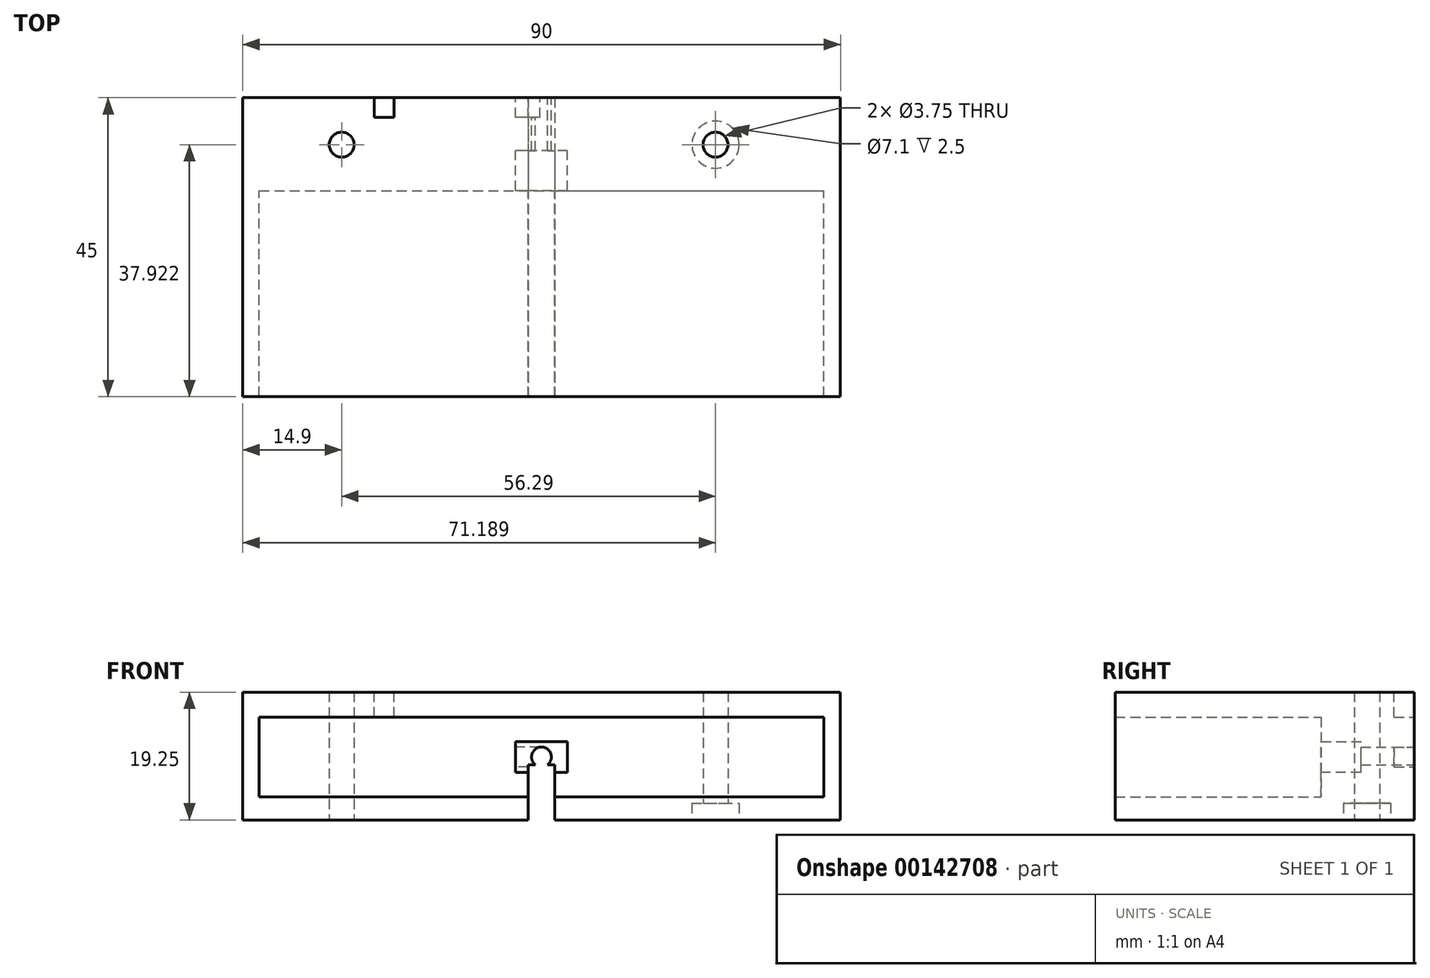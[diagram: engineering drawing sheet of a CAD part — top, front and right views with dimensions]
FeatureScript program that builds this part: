
annotation { "Feature Type Name" : "Feature", "Feature Type Description" : "" }
export const myFeature = defineFeature(function(context is Context, id is Id, definition is map)
    precondition{}
    {
        {
            var Q0;
            Q0=qCreatedBy(makeId("Front.planeOp"),FACE);
            var sketch = newSketch(context, id + "F0", { "sketchPlane" : qUnion([Q0])});
            skLineSegment(sketch, "E0.bottom", {"start": v(-59.7, 43.79) * mm, "end": v(25.3, 43.79) * mm});
            skLineSegment(sketch, "E0.top", {"start": v(-59.7, 31.79) * mm, "end": v(25.3, 31.79) * mm});
            skLineSegment(sketch, "E0.left", {"start": v(-59.7, 43.79) * mm, "end": v(-59.7, 31.79) * mm});
            skLineSegment(sketch, "E0.right", {"start": v(25.3, 43.79) * mm, "end": v(25.3, 31.79) * mm});
            skLineSegment(sketch, "E1.bottom", {"start": v(27.8, 28.3) * mm, "end": v(-62.2, 28.3) * mm});
            skLineSegment(sketch, "E1.top", {"start": v(27.8, 47.55) * mm, "end": v(-62.2, 47.55) * mm});
            skLineSegment(sketch, "E1.left", {"start": v(27.8, 28.3) * mm, "end": v(27.8, 47.55) * mm});
            skLineSegment(sketch, "E1.right", {"start": v(-62.2, 28.3) * mm, "end": v(-62.2, 47.55) * mm});
            skPoint(sketch, "E2", {"position": v(-59.7, 37.79) * mm});
            skPoint(sketch, "E3", {"position": v(-17.2, 43.79) * mm});
            skPoint(sketch, "E4", {"position": v(-17.2, 37.79) * mm});
            skLineSegment(sketch, "E5.bottom", {"start": v(-13.28, 35.46) * mm, "end": v(-21.13, 35.46) * mm});
            skLineSegment(sketch, "E5.top", {"start": v(-13.28, 40.12) * mm, "end": v(-21.13, 40.12) * mm});
            skLineSegment(sketch, "E5.left", {"start": v(-13.28, 35.46) * mm, "end": v(-13.28, 40.12) * mm});
            skLineSegment(sketch, "E5.right", {"start": v(-21.13, 35.46) * mm, "end": v(-21.13, 40.12) * mm});
            skCircle(sketch, "E6", {"center": v(-17.2, 37.79) * mm, "radius": 1.5 * mm});
            skSolve(sketch);
        }
        {
            var Q0;
            Q0=makeQuery(id+"F0.imprint","IMPRINT",FACE,{"disambiguationData":[TD([[makeQuery(id+"F0.imprint","IMPRINT",EDGE,{"derivedFrom":sQuery(id+"F0.wireOp",EDGE,"E0.bottom")}),1.0]])]});
            extrude(context, id + "F1", {"entities" : qUnion([Q0]), "offsetDistance" : 25 * mm, "depth" : 45 * mm});
        }
        {
            var Q0;
            Q0=makeQuery(id+"F0.imprint","IMPRINT",FACE,{"disambiguationData":[TD([[makeQuery(id+"F0.imprint","IMPRINT",EDGE,{"derivedFrom":sQuery(id+"F0.wireOp",EDGE,"E0.bottom")}),-1.0]])]});
            extrude(context, id + "F2", {"entities" : qUnion([Q0]), "operationType" : NewBodyOperationType.ADD, "offsetDistance" : 25 * mm, "depth" : 14 * mm});
        }
        {
            var Q0;
            Q0=makeQuery(id+"F0.imprint","IMPRINT",FACE,{"disambiguationData":[TD([[makeQuery(id+"F0.imprint","IMPRINT",EDGE,{"derivedFrom":sQuery(id+"F0.wireOp",EDGE,"E5.bottom")}),-1.0]])]});
            extrude(context, id + "F3", {"entities" : qUnion([Q0]), "operationType" : NewBodyOperationType.ADD, "depth" : 8 * mm});
        }
        {
            var Q0;
            Q0=makeQuery(id+"F1.opExtrude","SWEPT_FACE",FACE,{"disambiguationData":[OSD([sQuery(id+"F0.wireOp",EDGE,"E1.bottom")])]});
            cPlane(context, id + "F4", {"entities" : qUnion([Q0]), "cplaneType" : CPlaneType.OFFSET, "offset" : 0 * mm, "width" : 150 * mm, "height" : 150 * mm});
        }
        {
            var Q0;
            Q0=qCreatedBy(id+"F4.planeOp",FACE);
            var sketch = newSketch(context, id + "F5", { "sketchPlane" : qUnion([Q0])});
            skLineSegment(sketch, "E7.0.0", {"start": v(-62.2, 0) * mm, "end": v(27.8, 0) * mm});
            skLineSegment(sketch, "E7.0.1", {"start": v(27.8, 0) * mm, "end": v(27.8, 45) * mm});
            skLineSegment(sketch, "E7.0.2", {"start": v(27.8, 45) * mm, "end": v(-62.2, 45) * mm});
            skLineSegment(sketch, "E7.0.3", {"start": v(-62.2, 45) * mm, "end": v(-62.2, 0) * mm});
            skPoint(sketch, "E8", {"position": v(-62.2, 22.5) * mm});
            skPoint(sketch, "E9", {"position": v(-17.2, 45) * mm});
            skPoint(sketch, "E10", {"position": v(-17.2, 22.5) * mm});
            skLineSegment(sketch, "E11.bottom", {"start": v(-15.2, 15.94) * mm, "end": v(-19.2, 15.94) * mm});
            skLineSegment(sketch, "E11.top", {"start": v(-15.2, 74.06) * mm, "end": v(-19.2, 74.06) * mm});
            skLineSegment(sketch, "E11.left", {"start": v(-15.2, 15.94) * mm, "end": v(-15.2, 74.06) * mm});
            skLineSegment(sketch, "E11.right", {"start": v(-19.2, 15.94) * mm, "end": v(-19.2, 74.06) * mm});
            skLineSegment(sketch, "E12.bottom", {"start": v(-15.2, -0.81) * mm, "end": v(-19.2, -0.81) * mm});
            skLineSegment(sketch, "E12.top", {"start": v(-15.2, 90.81) * mm, "end": v(-19.2, 90.81) * mm});
            skLineSegment(sketch, "E12.left", {"start": v(-15.2, -0.81) * mm, "end": v(-15.2, 90.81) * mm});
            skLineSegment(sketch, "E12.right", {"start": v(-19.2, -0.81) * mm, "end": v(-19.2, 90.81) * mm});
            skSolve(sketch);
        }
        {
            var Q0;
            {var subQ5=sQuery(id+"F5.wireOp",EDGE,"E11.bottom");Q0=makeQuery(id+"F5.imprint","IMPRINT",FACE,{"disambiguationData":[TD([[makeQuery(id+"F5.imprint","IMPRINT",EDGE,{"derivedFrom":subQ5}),-1.0]])]});}
            extrude(context, id + "F6", {"entities" : qUnion([Q0]), "operationType" : NewBodyOperationType.REMOVE, "oppositeDirection" : true, "depth" : 3.07 * mm});
        }
        {
            var Q0;
            {var subQ0=sQuery(id+"F5.wireOp",EDGE,"E12.left");var subQ1=sQuery(id+"F5.wireOp",EDGE,"E7.0.2");var subQ2=makeQuery(id+"F5.imprint","INTERSECT",VERTEX,{"derivedFrom":[subQ1,subQ0]});Q0=makeQuery(id+"F5.imprint","IMPRINT",FACE,{"disambiguationData":[TD([[makeQuery(id+"F5.imprint","IMPRINT",EDGE,{"disambiguationData":[TD([[subQ2,-1.0]])],"derivedFrom":subQ1}),1.0]])]});}
            var Q1;
            {var subQ0=sQuery(id+"F5.wireOp",EDGE,"E11.bottom");Q1=makeQuery(id+"F5.imprint","IMPRINT",FACE,{"disambiguationData":[TD([[makeQuery(id+"F5.imprint","IMPRINT",EDGE,{"derivedFrom":subQ0}),1.0]])]});}
            extrude(context, id + "F7", {"entities" : qUnion([Q0, Q1]), "operationType" : NewBodyOperationType.REMOVE, "oppositeDirection" : true, "offsetDistance" : 25 * mm, "depth" : 8.28 * mm});
        }
        {
            var Q0;
            Q0=makeQuery(id+"F2.opExtrude","CAP_FACE",FACE,{"disambiguationData":[OSD([sQuery(id+"F0.wireOp",EDGE,"E0.bottom"),sQuery(id+"F0.wireOp",EDGE,"E0.top"),sQuery(id+"F0.wireOp",EDGE,"E0.left"),sQuery(id+"F0.wireOp",EDGE,"E0.right"),sQuery(id+"F0.wireOp",EDGE,"E5.bottom"),sQuery(id+"F0.wireOp",EDGE,"E5.top"),sQuery(id+"F0.wireOp",EDGE,"E5.left"),sQuery(id+"F0.wireOp",EDGE,"E5.right")])],"isStart":false});
            cPlane(context, id + "F8", {"entities" : qUnion([Q0]), "cplaneType" : CPlaneType.OFFSET, "offset" : 0 * mm, "width" : 150 * mm, "height" : 150 * mm});
        }
        {
            var Q0;
            Q0=qCreatedBy(id+"F8.planeOp",FACE);
            var sketch = newSketch(context, id + "F9", { "sketchPlane" : qUnion([Q0])});
            skPoint(sketch, "E13", {"position": v(-44.14, 37.92) * mm});
            skPoint(sketch, "E14", {"position": v(8.29, 37.92) * mm});
            skLineSegment(sketch, "E15.bottom", {"start": v(-44.36, 43.1) * mm, "end": v(-24.41, 43.1) * mm});
            skLineSegment(sketch, "E15.top", {"start": v(-44.36, 33.4) * mm, "end": v(-24.41, 33.4) * mm});
            skLineSegment(sketch, "E15.left", {"start": v(-44.36, 43.1) * mm, "end": v(-44.36, 33.4) * mm});
            skLineSegment(sketch, "E15.right", {"start": v(-24.41, 43.1) * mm, "end": v(-24.41, 33.4) * mm});
            skLineSegment(sketch, "E16.bottom", {"start": v(-10.07, 43.25) * mm, "end": v(11.6, 43.25) * mm});
            skLineSegment(sketch, "E16.top", {"start": v(-10.07, 33.55) * mm, "end": v(11.6, 33.55) * mm});
            skLineSegment(sketch, "E16.left", {"start": v(-10.07, 43.25) * mm, "end": v(-10.07, 33.55) * mm});
            skLineSegment(sketch, "E16.right", {"start": v(11.6, 43.25) * mm, "end": v(11.6, 33.55) * mm});
            skSolve(sketch);
        }
        {
            var Q0;
            Q0=qCreatedBy(id+"F4.planeOp",FACE);
            var sketch = newSketch(context, id + "F10", { "sketchPlane" : qUnion([Q0])});
            skLineSegment(sketch, "E17", {"start": v(-58.7, 7.08) * mm, "end": v(21.4, 7.08) * mm});
            skCircle(sketch, "E18", {"center": v(-47.3, 7.08) * mm, "radius": 1.87 * mm});
            skCircle(sketch, "E19", {"center": v(9, 7.08) * mm, "radius": 1.88 * mm});
            skCircle(sketch, "E20", {"center": v(-47.3, 7.08) * mm, "radius": 3.55 * mm});
            skCircle(sketch, "E21", {"center": v(9, 7.08) * mm, "radius": 3.55 * mm});
            skSolve(sketch);
        }
        {
            var Q0;
            {var subQ0=sQuery(id+"F10.wireOp",EDGE,"E18");var subQ1=sQuery(id+"F10.wireOp",EDGE,"E17");var subQ2=makeQuery(id+"F10.imprint","INTERSECT",VERTEX,{"disambiguationData":[OD(0.0)],"derivedFrom":[subQ1,subQ0]});Q0=makeQuery(id+"F10.imprint","IMPRINT",FACE,{"disambiguationData":[TD([[makeQuery(id+"F10.imprint","IMPRINT",EDGE,{"disambiguationData":[TD([[subQ2,-1.0]])],"derivedFrom":subQ1}),1.0]])]});}
            var Q1;
            {var subQ0=sQuery(id+"F10.wireOp",EDGE,"E18");var subQ1=sQuery(id+"F10.wireOp",EDGE,"E17");var subQ2=makeQuery(id+"F10.imprint","INTERSECT",VERTEX,{"disambiguationData":[OD(0.0)],"derivedFrom":[subQ1,subQ0]});Q1=makeQuery(id+"F10.imprint","IMPRINT",FACE,{"disambiguationData":[TD([[makeQuery(id+"F10.imprint","IMPRINT",EDGE,{"disambiguationData":[TD([[subQ2,-1.0]])],"derivedFrom":subQ1}),-1.0]])]});}
            var Q2;
            {var subQ0=sQuery(id+"F10.wireOp",EDGE,"E19");var subQ1=sQuery(id+"F10.wireOp",EDGE,"E17");var subQ2=makeQuery(id+"F10.imprint","INTERSECT",VERTEX,{"disambiguationData":[OD(0.0)],"derivedFrom":[subQ1,subQ0]});Q2=makeQuery(id+"F10.imprint","IMPRINT",FACE,{"disambiguationData":[TD([[makeQuery(id+"F10.imprint","IMPRINT",EDGE,{"disambiguationData":[TD([[subQ2,-1.0]])],"derivedFrom":subQ1}),1.0]])]});}
            var Q3;
            {var subQ0=sQuery(id+"F10.wireOp",EDGE,"E19");var subQ1=sQuery(id+"F10.wireOp",EDGE,"E17");var subQ2=makeQuery(id+"F10.imprint","INTERSECT",VERTEX,{"disambiguationData":[OD(0.0)],"derivedFrom":[subQ1,subQ0]});Q3=makeQuery(id+"F10.imprint","IMPRINT",FACE,{"disambiguationData":[TD([[makeQuery(id+"F10.imprint","IMPRINT",EDGE,{"disambiguationData":[TD([[subQ2,-1.0]])],"derivedFrom":subQ1}),-1.0]])]});}
            var Q4;
            Q4=sQuery(id+"F10.wireOp",EDGE,"E18");
            var Q5;
            Q5=sQuery(id+"F10.wireOp",EDGE,"E19");
            extrude(context, id + "F11", {"entities" : qUnion([Q0, Q1, Q2, Q3]), "operationType" : NewBodyOperationType.REMOVE, "surfaceEntities" : qUnion([Q4, Q5]), "oppositeDirection" : true, "depth" : 23.33 * mm});
        }
        {
            var Q0;
            {var subQ0=sQuery(id+"F10.wireOp",EDGE,"E21");var subQ1=sQuery(id+"F10.wireOp",EDGE,"E17");var subQ2=makeQuery(id+"F10.imprint","INTERSECT",VERTEX,{"disambiguationData":[OD(0.0)],"derivedFrom":[subQ1,subQ0]});Q0=makeQuery(id+"F10.imprint","IMPRINT",FACE,{"disambiguationData":[TD([[makeQuery(id+"F10.imprint","IMPRINT",EDGE,{"disambiguationData":[TD([[subQ2,-1.0]])],"derivedFrom":subQ1}),-1.0]])]});}
            var Q1;
            {var subQ0=sQuery(id+"F10.wireOp",EDGE,"E21");var subQ1=sQuery(id+"F10.wireOp",EDGE,"E17");var subQ2=makeQuery(id+"F10.imprint","INTERSECT",VERTEX,{"disambiguationData":[OD(0.0)],"derivedFrom":[subQ1,subQ0]});Q1=makeQuery(id+"F10.imprint","IMPRINT",FACE,{"disambiguationData":[TD([[makeQuery(id+"F10.imprint","IMPRINT",EDGE,{"disambiguationData":[TD([[subQ2,-1.0]])],"derivedFrom":subQ1}),1.0]])]});}
            var Q2;
            {var subQ0=sQuery(id+"F10.wireOp",EDGE,"E20");var subQ1=sQuery(id+"F10.wireOp",EDGE,"E17");var subQ2=makeQuery(id+"F10.imprint","INTERSECT",VERTEX,{"disambiguationData":[OD(0.0)],"derivedFrom":[subQ1,subQ0]});Q2=makeQuery(id+"F10.imprint","IMPRINT",FACE,{"disambiguationData":[TD([[makeQuery(id+"F10.imprint","IMPRINT",EDGE,{"disambiguationData":[TD([[subQ2,-1.0]])],"derivedFrom":subQ1}),-1.0]])]});}
            var Q3;
            {var subQ0=sQuery(id+"F10.wireOp",EDGE,"E20");var subQ1=sQuery(id+"F10.wireOp",EDGE,"E17");var subQ2=makeQuery(id+"F10.imprint","INTERSECT",VERTEX,{"disambiguationData":[OD(0.0)],"derivedFrom":[subQ1,subQ0]});Q3=makeQuery(id+"F10.imprint","IMPRINT",FACE,{"disambiguationData":[TD([[makeQuery(id+"F10.imprint","IMPRINT",EDGE,{"disambiguationData":[TD([[subQ2,-1.0]])],"derivedFrom":subQ1}),1.0]])]});}
            extrude(context, id + "F12", {"entities" : qUnion([Q0, Q1, Q2, Q3]), "operationType" : NewBodyOperationType.REMOVE, "oppositeDirection" : true, "depth" : 2.5 * mm});
        }
        {
            var Q0;
            Q0=qCreatedBy(id+"F8.planeOp",FACE);
            var sketch = newSketch(context, id + "F13", { "sketchPlane" : qUnion([Q0])});
            skCircle(sketch, "E22", {"center": v(-50.6, 38.04) * mm, "radius": 3.5 * mm});
            skCircle(sketch, "E23", {"center": v(-50.6, 38.04) * mm, "radius": 1.85 * mm});
            skCircle(sketch, "E24", {"center": v(0, 38.44) * mm, "radius": 3.5 * mm});
            skCircle(sketch, "E25", {"center": v(0, 38.44) * mm, "radius": 1.85 * mm});
            skSolve(sketch);
        }
        {
            var Q0;
            Q0=makeQuery(id+"F0.imprint","IMPRINT",FACE,{"disambiguationData":[TD([[makeQuery(id+"F0.imprint","IMPRINT",EDGE,{"derivedFrom":sQuery(id+"F0.wireOp",EDGE,"E0.bottom")}),-1.0]])]});
            var sketch = newSketch(context, id + "F14", { "sketchPlane" : qUnion([Q0])});
            skLineSegment(sketch, "E26.bottom", {"start": v(-17.22, 39.27) * mm, "end": v(-39.42, 39.27) * mm});
            skLineSegment(sketch, "E26.top", {"start": v(-17.22, 36.27) * mm, "end": v(-42.42, 36.27) * mm});
            skLineSegment(sketch, "E26.left", {"start": v(-17.22, 39.27) * mm, "end": v(-17.22, 36.27) * mm});
            skLineSegment(sketch, "E26.right", {"start": v(-42.42, 39.27) * mm, "end": v(-42.42, 36.27) * mm});
            skLineSegment(sketch, "E27.bottom", {"start": v(-42.42, 36.27) * mm, "end": v(-39.42, 36.27) * mm});
            skLineSegment(sketch, "E27.top", {"start": v(-42.42, 48.2) * mm, "end": v(-39.42, 48.2) * mm});
            skLineSegment(sketch, "E27.left", {"start": v(-42.42, 36.27) * mm, "end": v(-42.42, 48.2) * mm});
            skLineSegment(sketch, "E27.right", {"start": v(-39.42, 39.27) * mm, "end": v(-39.42, 48.2) * mm});
            skSolve(sketch);
        }
        {
            var Q0;
            {var subQ1=sQuery(id+"F14.wireOp",EDGE,"E27.bottom");Q0=makeQuery(id+"F14.imprint","IMPRINT",FACE,{"disambiguationData":[TD([[makeQuery(id+"F14.imprint","IMPRINT",EDGE,{"derivedFrom":subQ1}),1.0]])]});}
            var Q1;
            {var subQ0=sQuery(id+"F14.wireOp",EDGE,"E27.top");Q1=makeQuery(id+"F14.imprint","IMPRINT",FACE,{"disambiguationData":[TD([[makeQuery(id+"F14.imprint","IMPRINT",EDGE,{"derivedFrom":subQ0}),-1.0]])]});}
            var Q2;
            {var subQ0=sQuery(id+"F14.wireOp",EDGE,"E26.left");Q2=makeQuery(id+"F14.imprint","IMPRINT",FACE,{"disambiguationData":[TD([[makeQuery(id+"F14.imprint","IMPRINT",EDGE,{"derivedFrom":subQ0}),-1.0]])]});}
            extrude(context, id + "F15", {"entities" : qUnion([Q0, Q1, Q2]), "operationType" : NewBodyOperationType.REMOVE, "depth" : 3 * mm, "offsetDistance" : 25 * mm});
        }
    });
